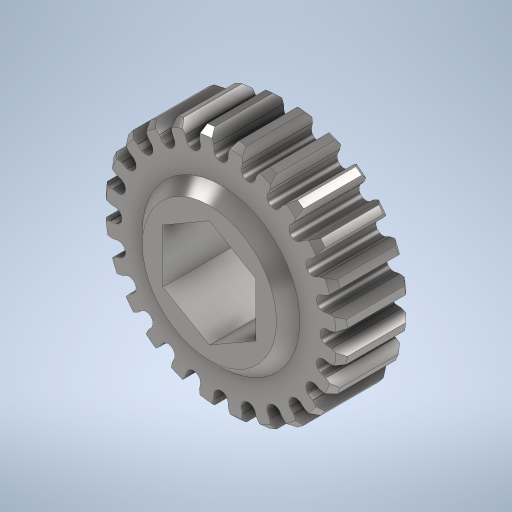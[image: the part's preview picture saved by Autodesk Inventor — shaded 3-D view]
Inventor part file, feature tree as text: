
AUTODESK INVENTOR PART (.ipt)
format: ipt  version: 2024 (Build 280153000, 153)  size: 737,280 bytes
history: native  units: in
note: dims shown in document units (in); Inventor stores cm internally (conversion verified against a paired STEP export)
features: mirror x1
ambient origin geometry x8: Origin, YZ Plane, XZ Plane, XY Plane, X Axis, Y Axis, Z Axis, Center Point
bodies: Solid1 (feature_tree)
feature tree (1):
  mirror  "Mirror6"
